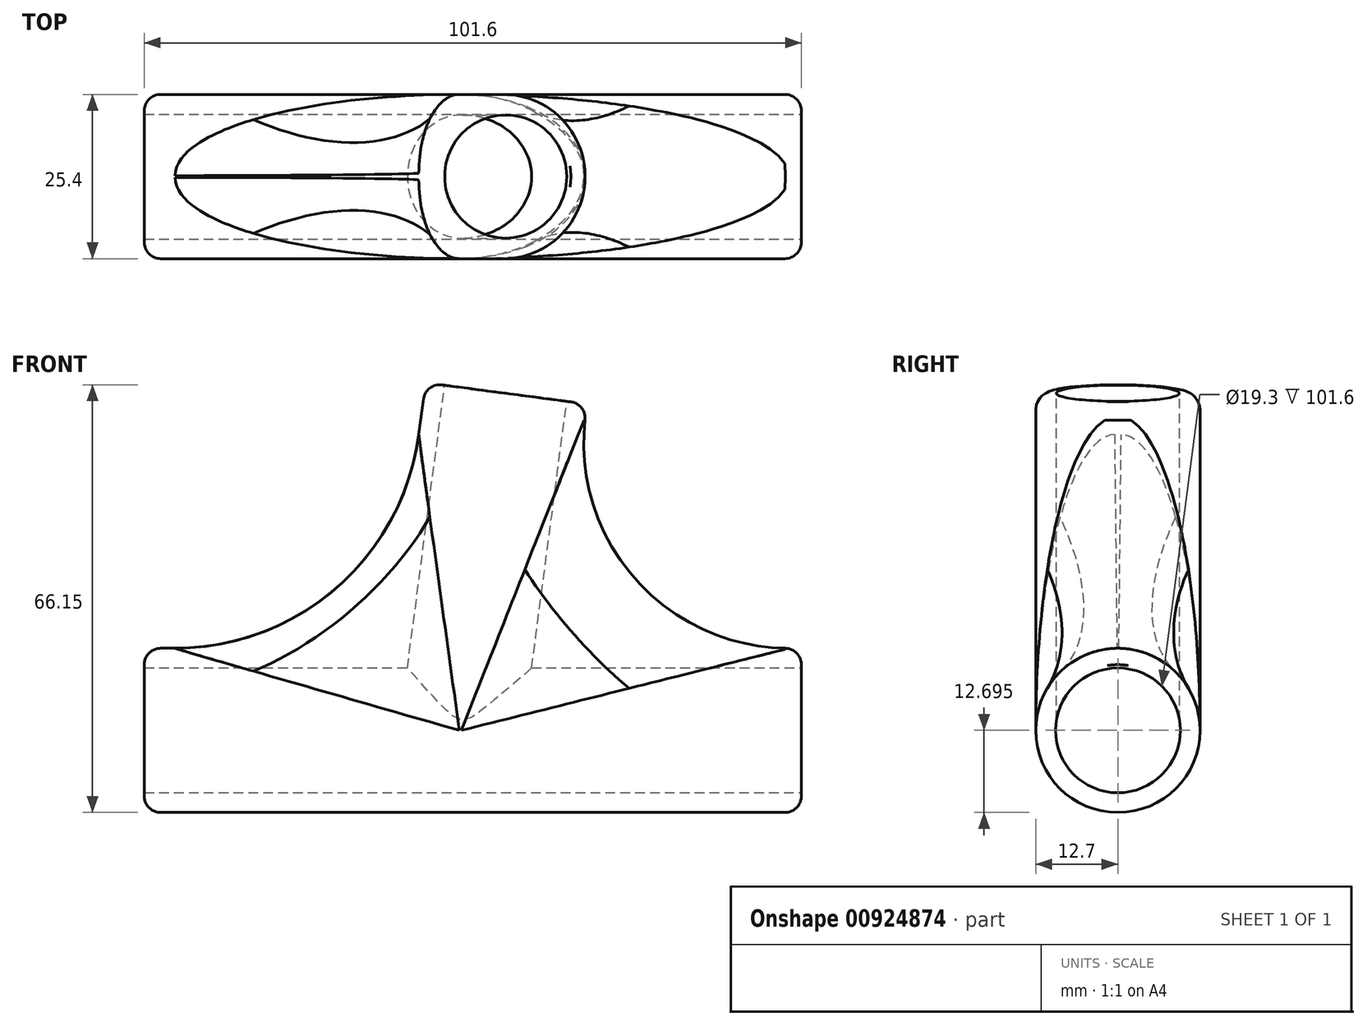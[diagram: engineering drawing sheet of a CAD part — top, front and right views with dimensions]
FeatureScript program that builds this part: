
annotation { "Feature Type Name" : "Feature", "Feature Type Description" : "" }
export const myFeature = defineFeature(function(context is Context, id is Id, definition is map)
    precondition{}
    {
        {
            var Q0;
            Q0=qCreatedBy(makeId("Front.planeOp"),FACE);
            var sketch = newSketch(context, id + "F0", { "sketchPlane" : qUnion([Q0])});
            skLineSegment(sketch, "E0.bottom", {"start": v(-42.97, 8.38) * mm, "end": v(-4.87, 8.38) * mm});
            skLineSegment(sketch, "E0.top", {"start": v(-42.97, -17.02) * mm, "end": v(58.63, -17.02) * mm});
            skLineSegment(sketch, "E0.left", {"start": v(-42.97, 8.38) * mm, "end": v(-42.97, -17.02) * mm});
            skLineSegment(sketch, "E0.right", {"start": v(58.63, 8.38) * mm, "end": v(58.63, -17.02) * mm});
            skLineSegment(sketch, "E1.right", {"start": v(25.5, 46.15) * mm, "end": v(20.53, 8.38) * mm});
            skLineSegment(sketch, "E2.trimOffspring", {"start": v(20.53, 8.38) * mm, "end": v(58.63, 8.38) * mm});
            skLineSegment(sketch, "E3", {"start": v(-4.87, 8.38) * mm, "end": v(0.53, 49.44) * mm});
            skLineSegment(sketch, "E4", {"start": v(25.5, 46.15) * mm, "end": v(0.53, 49.44) * mm});
            skSolve(sketch);
        }
        {
            var Q0;
            Q0 = qSketchRegion(id + "F0", true);
            extrude(context, id + "F1", {"entities" : qUnion([Q0]), "depth" : 25.4 * mm, "offsetDistance" : 25.4 * mm});
        }
        {
            var Q0;
            Q0=makeQuery(id+"F1.opExtrude","CAP_EDGE",EDGE,{"disambiguationData":[OSD([sQuery(id+"F0.wireOp",EDGE,"E0.bottom")])],"isStart":true});
            var Q1;
            Q1=makeQuery(id+"F1.opExtrude","CAP_EDGE",EDGE,{"disambiguationData":[OSD([sQuery(id+"F0.wireOp",EDGE,"E1.right")])],"isStart":true});
            var Q2;
            Q2=makeQuery(id+"F1.opExtrude","CAP_EDGE",EDGE,{"disambiguationData":[OSD([sQuery(id+"F0.wireOp",EDGE,"E2.trimOffspring")])],"isStart":true});
            var Q3;
            Q3=makeQuery(id+"F1.opExtrude","CAP_EDGE",EDGE,{"disambiguationData":[OSD([sQuery(id+"F0.wireOp",EDGE,"E0.bottom")])],"isStart":false});
            var Q4;
            Q4=makeQuery(id+"F1.opExtrude","CAP_EDGE",EDGE,{"disambiguationData":[OSD([sQuery(id+"F0.wireOp",EDGE,"E1.left")])],"isStart":false});
            var Q5;
            Q5=makeQuery(id+"F1.opExtrude","CAP_EDGE",EDGE,{"disambiguationData":[OSD([sQuery(id+"F0.wireOp",EDGE,"E2.trimOffspring")])],"isStart":false});
            var Q6;
            Q6=makeQuery(id+"F1.opExtrude","CAP_EDGE",EDGE,{"disambiguationData":[OSD([sQuery(id+"F0.wireOp",EDGE,"E1.right")])],"isStart":false});
            var Q7;
            Q7=makeQuery(id+"F1.opExtrude","CAP_EDGE",EDGE,{"disambiguationData":[OSD([sQuery(id+"F0.wireOp",EDGE,"E1.left")])],"isStart":true});
            fillet(context, id + "F2", {"entities" : qUnion([Q0, Q1, Q2, Q3, Q4, Q5, Q6, Q7]), "radius" : 12.7 * mm, "tangentPropagation" : true, "allowEdgeOverflow" : false});
        }
        {
            var Q0;
            Q0=makeQuery(id+"F1.opExtrude","CAP_EDGE",EDGE,{"disambiguationData":[OSD([sQuery(id+"F0.wireOp",EDGE,"E1.right")])],"isStart":false});
            var Q1;
            Q1=makeQuery(id+"F1.opExtrude","CAP_EDGE",EDGE,{"disambiguationData":[OSD([sQuery(id+"F0.wireOp",EDGE,"E0.top")])],"isStart":false});
            var Q2;
            Q2=makeQuery(id+"F1.opExtrude","CAP_EDGE",EDGE,{"disambiguationData":[OSD([sQuery(id+"F0.wireOp",EDGE,"E0.top")])],"isStart":true});
            fillet(context, id + "F3", {"entities" : qUnion([Q0, Q1, Q2]), "radius" : 12.7 * mm, "tangentPropagation" : true, "allowEdgeOverflow" : false});
        }
        {
            var Q0;
            Q0=makeQuery(id+"F3.opFillet","BLEND_EDGE",EDGE,{"blendedFrom":[makeQuery(id+"F1.opExtrude","CAP_EDGE",EDGE,{"disambiguationData":[OSD([sQuery(id+"F0.wireOp",EDGE,"E1.right")])],"isStart":false}),makeQuery(id+"F2.opFillet","BLEND_FACE",FACE,{"disambiguationData":[OSD([sQuery(id+"F0.wireOp",EDGE,"E0.bottom")])]})],"blendedInto":[makeQuery(id+"F2.opFillet","BLEND_FACE",FACE,{"disambiguationData":[OSD([sQuery(id+"F0.wireOp",EDGE,"E0.bottom")])]})]});
            var Q1;
            Q1=makeQuery(id+"F2.opFillet","BLEND_EDGE",EDGE,{"blendedFrom":[makeQuery(id+"F1.opExtrude","CAP_EDGE",EDGE,{"disambiguationData":[OSD([sQuery(id+"F0.wireOp",EDGE,"E1.right")])],"isStart":true}),makeQuery(id+"F1.opExtrude","CAP_EDGE",EDGE,{"disambiguationData":[OSD([sQuery(id+"F0.wireOp",EDGE,"E2.trimOffspring")])],"isStart":true})],"blendedInto":[]});
            var Q2;
            Q2=makeQuery(id+"F2.opFillet","BLEND_EDGE",EDGE,{"blendedFrom":[makeQuery(id+"F1.opExtrude","CAP_EDGE",EDGE,{"disambiguationData":[OSD([sQuery(id+"F0.wireOp",EDGE,"E0.bottom")])],"isStart":true}),makeQuery(id+"F1.opExtrude","CAP_EDGE",EDGE,{"disambiguationData":[OSD([sQuery(id+"F0.wireOp",EDGE,"E1.left")])],"isStart":true})],"blendedInto":[]});
            fillet(context, id + "F4", {"entities" : qUnion([Q0, Q1, Q2]), "radius" : 31.75 * mm, "tangentPropagation" : true, "allowEdgeOverflow" : false});
        }
        {
            var Q0;
            Q0=makeQuery(id+"F1.opExtrude","SWEPT_FACE",FACE,{"disambiguationData":[OSD([sQuery(id+"F0.wireOp",EDGE,"E0.right")])]});
            var sketch = newSketch(context, id + "F5", { "sketchPlane" : qUnion([Q0])});
            skCircle(sketch, "E5", {"center": v(-12.7, -4.32) * mm, "radius": 9.65 * mm});
            skSolve(sketch);
        }
        {
            var Q0;
            Q0=makeQuery(id+"F5.imprint","IMPRINT",FACE,{"disambiguationData":[TD([[makeQuery(id+"F5.imprint","IMPRINT",EDGE,{"derivedFrom":sQuery(id+"F5.wireOp",EDGE,"E5")}),1.0]])]});
            extrude(context, id + "F6", {"entities" : qUnion([Q0]), "operationType" : NewBodyOperationType.REMOVE, "oppositeDirection" : true, "depth" : 151.13 * mm, "offsetDistance" : 25.4 * mm});
        }
        {
            var Q0;
            Q0=makeQuery(id+"F2.opFillet","BLEND_EDGE",EDGE,{"blendedFrom":[makeQuery(id+"F1.opExtrude","CAP_EDGE",EDGE,{"disambiguationData":[OSD([sQuery(id+"F0.wireOp",EDGE,"E1.left")])],"isStart":true}),makeQuery(id+"F1.opExtrude","SWEPT_FACE",FACE,{"disambiguationData":[OSD([sQuery(id+"F0.wireOp",EDGE,"E1.bottom")])]})],"blendedInto":[makeQuery(id+"F1.opExtrude","SWEPT_FACE",FACE,{"disambiguationData":[OSD([sQuery(id+"F0.wireOp",EDGE,"E1.bottom")])]})]});
            var Q1;
            Q1=makeQuery(id+"F2.opFillet","BLEND_EDGE",EDGE,{"blendedFrom":[makeQuery(id+"F1.opExtrude","CAP_EDGE",EDGE,{"disambiguationData":[OSD([sQuery(id+"F0.wireOp",EDGE,"E0.top")])],"isStart":true}),makeQuery(id+"F1.opExtrude","SWEPT_FACE",FACE,{"disambiguationData":[OSD([sQuery(id+"F0.wireOp",EDGE,"E0.right")])]})],"blendedInto":[makeQuery(id+"F1.opExtrude","SWEPT_FACE",FACE,{"disambiguationData":[OSD([sQuery(id+"F0.wireOp",EDGE,"E0.right")])]})]});
            var Q2;
            Q2=makeQuery(id+"F2.opFillet","BLEND_EDGE",EDGE,{"blendedFrom":[makeQuery(id+"F1.opExtrude","CAP_EDGE",EDGE,{"disambiguationData":[OSD([sQuery(id+"F0.wireOp",EDGE,"E0.bottom")])],"isStart":true}),makeQuery(id+"F1.opExtrude","SWEPT_FACE",FACE,{"disambiguationData":[OSD([sQuery(id+"F0.wireOp",EDGE,"E0.left")])]})],"blendedInto":[makeQuery(id+"F1.opExtrude","SWEPT_FACE",FACE,{"disambiguationData":[OSD([sQuery(id+"F0.wireOp",EDGE,"E0.left")])]})]});
            var Q3;
            Q3=makeQuery(id+"F2.opFillet","BLEND_EDGE",EDGE,{"blendedFrom":[makeQuery(id+"F1.opExtrude","CAP_EDGE",EDGE,{"disambiguationData":[OSD([sQuery(id+"F0.wireOp",EDGE,"E2.trimOffspring")])],"isStart":true}),makeQuery(id+"F1.opExtrude","SWEPT_FACE",FACE,{"disambiguationData":[OSD([sQuery(id+"F0.wireOp",EDGE,"E0.right")])]})],"blendedInto":[makeQuery(id+"F1.opExtrude","SWEPT_FACE",FACE,{"disambiguationData":[OSD([sQuery(id+"F0.wireOp",EDGE,"E0.right")])]})]});
            var Q4;
            Q4=makeQuery(id+"F3.opFillet","BLEND_EDGE",EDGE,{"blendedFrom":[makeQuery(id+"F1.opExtrude","CAP_EDGE",EDGE,{"disambiguationData":[OSD([sQuery(id+"F0.wireOp",EDGE,"E0.top")])],"isStart":false}),makeQuery(id+"F1.opExtrude","SWEPT_FACE",FACE,{"disambiguationData":[OSD([sQuery(id+"F0.wireOp",EDGE,"E0.right")])]})],"blendedInto":[makeQuery(id+"F1.opExtrude","SWEPT_FACE",FACE,{"disambiguationData":[OSD([sQuery(id+"F0.wireOp",EDGE,"E0.right")])]})]});
            fillet(context, id + "F7", {"entities" : qUnion([Q0, Q1, Q2, Q3, Q4]), "radius" : 2.54 * mm, "tangentPropagation" : true, "allowEdgeOverflow" : false});
        }
        {
            var Q0;
            Q0=makeQuery(id+"F1.opExtrude","SWEPT_FACE",FACE,{"disambiguationData":[OSD([sQuery(id+"F0.wireOp",EDGE,"E4")])]});
            var sketch = newSketch(context, id + "F8", { "sketchPlane" : qUnion([Q0])});
            skCircle(sketch, "E6", {"center": v(6.56, -12.7) * mm, "radius": 9.53 * mm});
            skSolve(sketch);
        }
        {
            var Q0;
            Q0=makeQuery(id+"F8.imprint","IMPRINT",FACE,{"disambiguationData":[TD([[makeQuery(id+"F8.imprint","IMPRINT",EDGE,{"derivedFrom":sQuery(id+"F8.wireOp",EDGE,"E6")}),1.0]])]});
            extrude(context, id + "F9", {"entities" : qUnion([Q0]), "operationType" : NewBodyOperationType.REMOVE, "oppositeDirection" : true, "depth" : 51.05 * mm, "offsetDistance" : 25.4 * mm});
        }
        {
            var Q0;
            Q0=makeQuery(id+"F1.opExtrude","CAP_EDGE",EDGE,{"disambiguationData":[OSD([sQuery(id+"F0.wireOp",EDGE,"E3")])],"isStart":true});
            var Q1;
            Q1=makeQuery(id+"F1.opExtrude","CAP_EDGE",EDGE,{"disambiguationData":[OSD([sQuery(id+"F0.wireOp",EDGE,"E3")])],"isStart":false});
            fillet(context, id + "F10", {"entities" : qUnion([Q0, Q1]), "radius" : 12.2 * mm, "tangentPropagation" : true, "allowEdgeOverflow" : false});
        }
        {
            var Q0;
            Q0=makeQuery(id+"F10.opFillet","BLEND_EDGE",EDGE,{"blendedFrom":[makeQuery(id+"F1.opExtrude","CAP_EDGE",EDGE,{"disambiguationData":[OSD([sQuery(id+"F0.wireOp",EDGE,"E3")])],"isStart":true}),makeQuery(id+"F3.opFillet","MERGE",FACE,{"derivedFrom":[makeQuery(id+"F2.opFillet","BLEND_FACE",FACE,{"disambiguationData":[OSD([sQuery(id+"F0.wireOp",EDGE,"E0.bottom")])]}),makeQuery(id+"F2.opFillet","BLEND_FACE",FACE,{"disambiguationData":[OSD([sQuery(id+"F0.wireOp",EDGE,"E2.trimOffspring")])]})]})],"blendedInto":[makeQuery(id+"F3.opFillet","MERGE",FACE,{"derivedFrom":[makeQuery(id+"F2.opFillet","BLEND_FACE",FACE,{"disambiguationData":[OSD([sQuery(id+"F0.wireOp",EDGE,"E0.bottom")])]}),makeQuery(id+"F2.opFillet","BLEND_FACE",FACE,{"disambiguationData":[OSD([sQuery(id+"F0.wireOp",EDGE,"E2.trimOffspring")])]})]})]});
            var Q1;
            Q1=makeQuery(id+"F10.opFillet","BLEND_EDGE",EDGE,{"blendedFrom":[makeQuery(id+"F1.opExtrude","CAP_EDGE",EDGE,{"disambiguationData":[OSD([sQuery(id+"F0.wireOp",EDGE,"E3")])],"isStart":false}),makeQuery(id+"F3.opFillet","MERGE",FACE,{"derivedFrom":[makeQuery(id+"F2.opFillet","BLEND_FACE",FACE,{"disambiguationData":[OSD([sQuery(id+"F0.wireOp",EDGE,"E0.bottom")])]}),makeQuery(id+"F2.opFillet","BLEND_FACE",FACE,{"disambiguationData":[OSD([sQuery(id+"F0.wireOp",EDGE,"E2.trimOffspring")])]})]})],"blendedInto":[makeQuery(id+"F3.opFillet","MERGE",FACE,{"derivedFrom":[makeQuery(id+"F2.opFillet","BLEND_FACE",FACE,{"disambiguationData":[OSD([sQuery(id+"F0.wireOp",EDGE,"E0.bottom")])]}),makeQuery(id+"F2.opFillet","BLEND_FACE",FACE,{"disambiguationData":[OSD([sQuery(id+"F0.wireOp",EDGE,"E2.trimOffspring")])]})]})]});
            fillet(context, id + "F11", {"entities" : qUnion([Q0, Q1]), "radius" : 38.02 * mm, "tangentPropagation" : true, "allowEdgeOverflow" : false});
        }
        {
            var Q0;
            Q0=makeQuery(id+"F10.opFillet","BLEND_EDGE",EDGE,{"blendedFrom":[makeQuery(id+"F1.opExtrude","CAP_EDGE",EDGE,{"disambiguationData":[OSD([sQuery(id+"F0.wireOp",EDGE,"E3")])],"isStart":true}),makeQuery(id+"F1.opExtrude","SWEPT_FACE",FACE,{"disambiguationData":[OSD([sQuery(id+"F0.wireOp",EDGE,"E4")])]})],"blendedInto":[makeQuery(id+"F1.opExtrude","SWEPT_FACE",FACE,{"disambiguationData":[OSD([sQuery(id+"F0.wireOp",EDGE,"E4")])]})]});
            fillet(context, id + "F12", {"entities" : qUnion([Q0]), "radius" : 2.54 * mm, "tangentPropagation" : true, "allowEdgeOverflow" : false});
        }
    });
